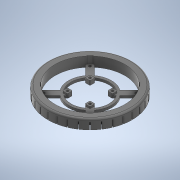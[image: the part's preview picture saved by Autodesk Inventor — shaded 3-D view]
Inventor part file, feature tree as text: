
AUTODESK INVENTOR PART (.ipt)
format: ipt  version: 2020 (Build 240168000, 168)  size: 1,406,464 bytes
history: native  units: mm
features: projected_geometry x13, extrude x12, sketch x10, pattern_circular x5, fillet x4, other x1
ambient origin geometry x8: Origin, YZ Plane, XZ Plane, XY Plane, X Axis, Y Axis, Z Axis, Center Point
bodies: Body1 (feature_tree)
feature tree (45):
  other  "Твердое тело1"
  sketch  "Эскиз1"
  extrude  "Выдавливание1"  Depth=88.0mm
  extrude  "Выдавливание2"  Depth=5.7mm
  pattern_circular  "Круговой массив1"  [2 undecoded]
  extrude  "Выдавливание3"  Depth=5.4mm
  fillet  "Сопряжение1"  Radius=98.0mm
  extrude  "Выдавливание4"  Depth=84.0mm
  pattern_circular  "Круговой массив2"  [2 undecoded]
  fillet  "Сопряжение2"  Radius=98.0mm
  extrude  "Выдавливание5"  Depth=84.0mm
  pattern_circular  "Круговой массив3"  [2 undecoded]
  extrude  "Выдавливание6"  Depth=10.0mm TaperAngle=0.0deg
  fillet  "Сопряжение3"  Radius=320.0mm
  sketch  "Эскиз6"
  extrude  "Выдавливание7"  Depth=2.0mm
  pattern_circular  "Круговой массив4"  [2 undecoded]
  extrude  "Выдавливание8"  Depth=1.6mm TaperAngle=0.0deg
  extrude  "Выдавливание9"  Depth=2.0mm
  pattern_circular  "Круговой массив5"  [2 undecoded]
  fillet  "Сопряжение4"  Radius=320.0mm
  sketch  "Эскиз9"
  extrude  "Выдавливание10"  Depth=0.5mm
  extrude  "Выдавливание11"  Depth=78.0mm
  extrude  "Выдавливание12"  TaperAngle=135.0deg  [1 undecoded]
  sketch  "Эскиз2"
  sketch  "Эскиз3"
  projected_geometry  "Спроецированная петля1"
  sketch  "Эскиз4"
  projected_geometry  "Спроецированная петля2"
  sketch  "Эскиз5"
  projected_geometry  "Спроецированная петля3"
  projected_geometry  "Спроецированная петля4"
  projected_geometry  "Спроецированная петля5"
  projected_geometry  "Спроецированная петля6"
  projected_geometry  "Спроецированная петля7"
  sketch  "Эскиз7"
  sketch  "Эскиз8"
  projected_geometry  "Спроецированная петля8"
  projected_geometry  "Спроецированная петля9"
  projected_geometry  "Спроецированная петля10"
  projected_geometry  "Спроецированная петля11"
  projected_geometry  "Спроецированная петля12"
  projected_geometry  "Спроецированная петля13"
  sketch  "Эскиз10"
note: 11 required parameter values undecoded (feature->parameter linkage not recoverable at this tier; creation-order binding heuristic only, values carry confidence <= 0.55)
